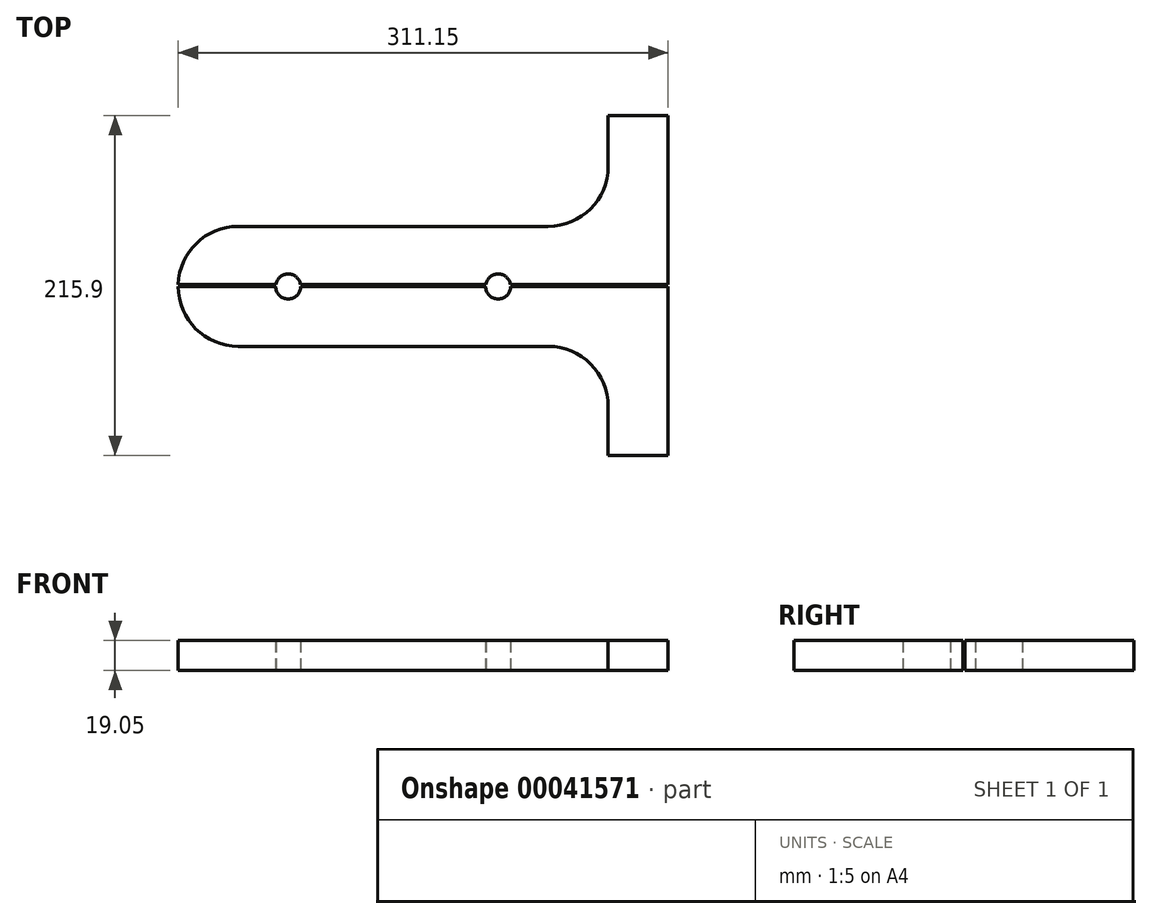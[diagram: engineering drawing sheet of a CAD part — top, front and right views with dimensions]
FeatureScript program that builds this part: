
annotation { "Feature Type Name" : "Feature", "Feature Type Description" : "" }
export const myFeature = defineFeature(function(context is Context, id is Id, definition is map)
    precondition{}
    {
        {
            var Q0;
            Q0=qCreatedBy(makeId("Top.planeOp"),FACE);
            var sketch = newSketch(context, id + "F3", { "sketchPlane" : qUnion([Q0])});
            skLineSegment(sketch, "E0.rect.bottom", {"start": v(-174.62, -107.95) * mm, "end": v(174.63, -107.95) * mm});
            skLineSegment(sketch, "E0.rect.top", {"start": v(-174.63, 107.95) * mm, "end": v(174.62, 107.95) * mm});
            skLineSegment(sketch, "E0.rect.left", {"start": v(-174.62, -107.95) * mm, "end": v(-174.63, 107.95) * mm});
            skLineSegment(sketch, "E0.rect.right", {"start": v(174.63, -107.95) * mm, "end": v(174.62, 107.95) * mm});
            skPoint(sketch, "E0.rect.middle", {"position": v(0, 0) * mm});
            skLineSegment(sketch, "E1.rect.bottom", {"start": v(-190.5, -0.63) * mm, "end": v(190.5, -0.63) * mm});
            skLineSegment(sketch, "E1.rect.top", {"start": v(-190.5, 0.64) * mm, "end": v(190.5, 0.64) * mm});
            skLineSegment(sketch, "E1.rect.left", {"start": v(-190.5, -0.63) * mm, "end": v(-190.5, 0.64) * mm});
            skLineSegment(sketch, "E1.rect.right", {"start": v(190.5, -0.63) * mm, "end": v(190.5, 0.64) * mm});
            skCircle(sketch, "E2", {"center": v(-66.68, -0.63) * mm, "radius": 7.94 * mm});
            skLineSegment(sketch, "E3", {"start": v(0, 107.95) * mm, "end": v(0, -107.95) * mm, "construction": true});
            skCircle(sketch, "E4.MirrorC", {"center": v(66.68, -0.63) * mm, "radius": 7.94 * mm});
            skLineSegment(sketch, "E5.rect.bottom", {"start": v(-136.53, -38.73) * mm, "end": v(136.53, -38.73) * mm});
            skLineSegment(sketch, "E5.rect.top", {"start": v(-136.53, 37.47) * mm, "end": v(136.53, 37.47) * mm});
            skLineSegment(sketch, "E5.rect.left", {"start": v(-136.53, -38.73) * mm, "end": v(-136.53, 37.47) * mm});
            skLineSegment(sketch, "E5.rect.right", {"start": v(136.53, -38.73) * mm, "end": v(136.53, 37.47) * mm});
            skPoint(sketch, "E5.rect.middle", {"position": v(0, -0.63) * mm});
            skLineSegment(sketch, "E6.bottom", {"start": v(-174.62, -107.95) * mm, "end": v(-136.53, -107.95) * mm});
            skLineSegment(sketch, "E6.top", {"start": v(-174.62, 107.95) * mm, "end": v(-136.53, 107.95) * mm});
            skLineSegment(sketch, "E6.left", {"start": v(-174.62, -107.95) * mm, "end": v(-174.62, 107.95) * mm});
            skLineSegment(sketch, "E6.right", {"start": v(-136.53, -107.95) * mm, "end": v(-136.53, 107.95) * mm});
            skLineSegment(sketch, "E7.MirrorCS", {"start": v(136.53, -107.95) * mm, "end": v(136.52, 107.95) * mm});
            skSolve(sketch);
        }
        {
            var Q0;
            {var subQ2=sQuery(id+"F3.wireOp",EDGE,"E6.top");Q0=makeQuery(id+"F3.imprint","IMPRINT",FACE,{"disambiguationData":[TD([[makeQuery(id+"F3.imprint","IMPRINT",EDGE,{"derivedFrom":subQ2}),-1.0]])]});}
            var Q1;
            {var subQ6=sQuery(id+"F3.wireOp",EDGE,"E6.bottom");Q1=makeQuery(id+"F3.imprint","IMPRINT",FACE,{"disambiguationData":[TD([[makeQuery(id+"F3.imprint","IMPRINT",EDGE,{"derivedFrom":subQ6}),1.0]])]});}
            var Q2;
            {var subQ3=sQuery(id+"F3.wireOp",EDGE,"E5.rect.bottom");Q2=makeQuery(id+"F3.imprint","IMPRINT",FACE,{"disambiguationData":[TD([[makeQuery(id+"F3.imprint","IMPRINT",EDGE,{"derivedFrom":subQ3}),1.0]])]});}
            var Q3;
            {var subQ3=sQuery(id+"F3.wireOp",EDGE,"E5.rect.top");Q3=makeQuery(id+"F3.imprint","IMPRINT",FACE,{"disambiguationData":[TD([[makeQuery(id+"F3.imprint","IMPRINT",EDGE,{"derivedFrom":subQ3}),-1.0]])]});}
            var Q4;
            {var subQ1=sQuery(id+"F3.wireOp",EDGE,"E0.rect.top");var subQ4=sQuery(id+"F3.wireOp",EDGE,"E0.rect.right");var subQ5=makeQuery(id+"F3.imprint","INTERSECT",VERTEX,{"derivedFrom":[subQ1,subQ4]});Q4=makeQuery(id+"F3.imprint","IMPRINT",FACE,{"disambiguationData":[TD([[makeQuery(id+"F3.imprint","IMPRINT",EDGE,{"disambiguationData":[TD([[subQ5,1.0]])],"derivedFrom":subQ1}),-1.0]])]});}
            var Q5;
            {var subQ4=sQuery(id+"F3.wireOp",EDGE,"E0.rect.bottom");var subQ6=sQuery(id+"F3.wireOp",EDGE,"E0.rect.right");var subQ7=makeQuery(id+"F3.imprint","INTERSECT",VERTEX,{"derivedFrom":[subQ4,subQ6]});Q5=makeQuery(id+"F3.imprint","IMPRINT",FACE,{"disambiguationData":[TD([[makeQuery(id+"F3.imprint","IMPRINT",EDGE,{"disambiguationData":[TD([[subQ7,1.0]])],"derivedFrom":subQ4}),1.0]])]});}
            extrude(context, id + "F0", {"entities" : qUnion([Q0, Q1, Q2, Q3, Q4, Q5]), "depth" : 19.05 * mm});
        }
        {
            var Q0;
            Q0=makeQuery(id+"F0.opExtrude","SWEPT_EDGE",EDGE,{"disambiguationData":[OSD([sQuery(id+"F3.wireOp",EDGE,"E5.rect.bottom"),sQuery(id+"F3.wireOp",EDGE,"E6.right")])]});
            var Q1;
            Q1=makeQuery(id+"F0.opExtrude","SWEPT_EDGE",EDGE,{"disambiguationData":[OSD([sQuery(id+"F3.wireOp",EDGE,"E5.rect.bottom"),sQuery(id+"F3.wireOp",EDGE,"E7.MirrorCS")])]});
            var Q2;
            Q2=makeQuery(id+"F0.opExtrude","SWEPT_EDGE",EDGE,{"disambiguationData":[OSD([sQuery(id+"F3.wireOp",EDGE,"E5.rect.top"),sQuery(id+"F3.wireOp",EDGE,"E7.MirrorCS")])]});
            var Q3;
            Q3=makeQuery(id+"F0.opExtrude","SWEPT_EDGE",EDGE,{"disambiguationData":[OSD([sQuery(id+"F3.wireOp",EDGE,"E5.rect.top"),sQuery(id+"F3.wireOp",EDGE,"E6.right")])]});
            fillet(context, id + "F1", {"entities" : qUnion([Q0, Q1, Q2, Q3]), "radius" : 38.1 * mm, "tangentPropagation" : true, "allowEdgeOverflow" : false});
        }
        {
            var Q0;
            Q0=makeQuery(id+"F0.opExtrude","SWEPT_BODY",BODY,{"disambiguationData":[OSD([sQuery(id+"F3.wireOp",EDGE,"E0.rect.bottom"),sQuery(id+"F3.wireOp",EDGE,"E0.rect.right"),sQuery(id+"F3.wireOp",EDGE,"E1.rect.bottom"),sQuery(id+"F3.wireOp",EDGE,"E2"),sQuery(id+"F3.wireOp",EDGE,"E4.MirrorC"),sQuery(id+"F3.wireOp",EDGE,"E5.rect.bottom"),sQuery(id+"F3.wireOp",EDGE,"E6.bottom"),sQuery(id+"F3.wireOp",EDGE,"E6.left"),sQuery(id+"F3.wireOp",EDGE,"E6.right"),sQuery(id+"F3.wireOp",EDGE,"E7.MirrorCS")])]});
            transform(context, id + "F2", {"entities" : qUnion([Q0]), "transformType" : TransformType.TRANSLATION_3D, "dx" : 0 * mm, "dy" : 0 * mm, "dz" : 0 * mm, "makeCopy" : true});
        }
    });
